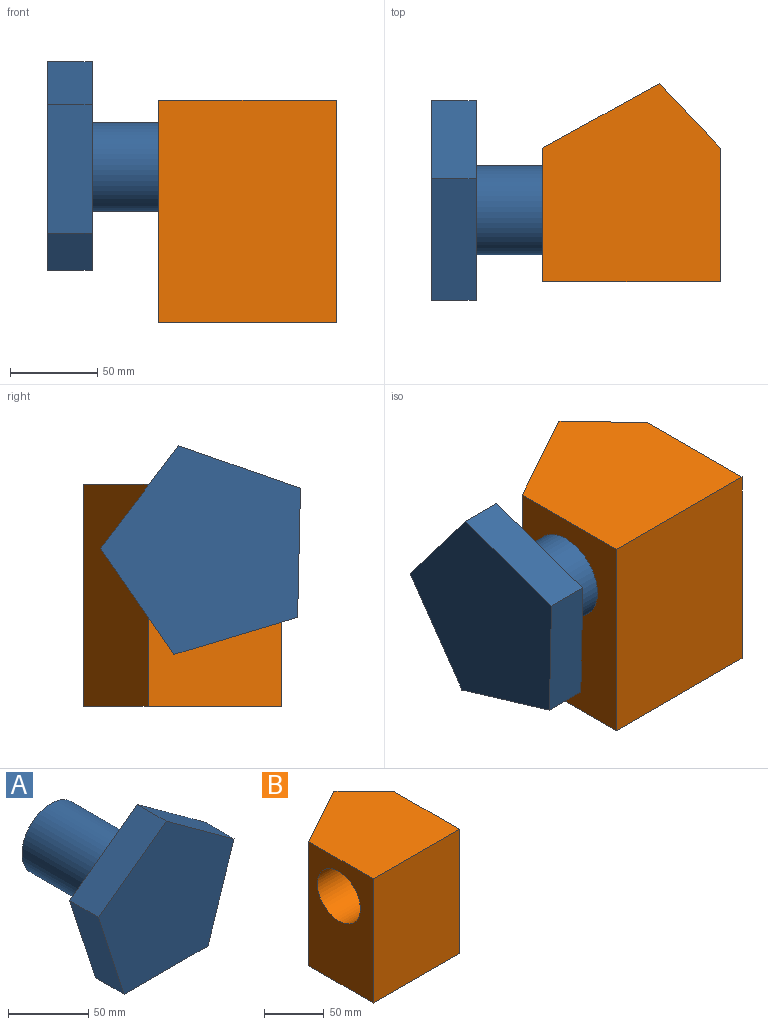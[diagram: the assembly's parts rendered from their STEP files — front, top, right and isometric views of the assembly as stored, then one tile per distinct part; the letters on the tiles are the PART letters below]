
ASSEMBLY  parts=2 mates=1
PART A: 9 faces, bbox 119.4x101.6x113.6 mm
  f0: cylinder r=25.4mm len=76.2mm, axis (0,1,0), area 12161mm2, adj f1,f8
  f1: plane 50.8x50.8mm, normal (0,1,0), area 2026.8mm2, adj f0
  f2: plane 70.2x25.4mm, normal (0.95,0,-0.31), area 1874.9mm2, adj f3,f6,f7,f8
  f3: plane 59.72x43.39mm, normal (0.59,0,0.81), area 1874.9mm2, adj f2,f4,f7,f8
  f4: plane 59.72x43.39mm, normal (-0.59,0,0.81), area 1874.9mm2, adj f3,f5,f7,f8
  f5: plane 70.2x25.4mm, normal (-0.95,0,-0.31), area 1874.9mm2, adj f4,f6,f7,f8
  f6: plane 73.82x25.4mm, normal (0,0,-1), area 1874.9mm2, adj f2,f5,f7,f8
  f7: plane 119.44x113.59mm, normal (0,-1,0), area 9374.7mm2, adj f2,f3,f4,f5,f6
  f8: plane 119.44x113.59mm, normal (0,1,0), area 7347.9mm2, adj f0,f2,f3,f4,f5,f6
PART B: 9 faces, bbox 101.6x113.1x127 mm
  f0: plane 127x76.2mm, normal (1,0,0), area 9677.4mm2, adj f1,f4,f5,f6
  f1: plane 127x36.89mm, normal (0.73,0.69,0), area 6451.6mm2, adj f0,f2,f5,f6
  f2: plane 127x66.68mm, normal (-0.48,0.88,0), area 9677.4mm2, adj f1,f3,f5,f6
  f3: plane 127x76.2mm, normal (-1,0,0), area 7650.6mm2, adj f2,f4,f5,f6,f7
  f4: plane 127x101.6mm, normal (0,-1,0), area 12903.2mm2, adj f0,f3,f5,f6
  f5: plane 113.09x101.6mm, normal (0,0,1), area 9615.9mm2, adj f0,f1,f2,f3,f4
  f6: plane 113.09x101.6mm, normal (0,0,-1), area 9615.9mm2, adj f0,f1,f2,f3,f4
  f7: cylinder r=25.4mm len=50.8mm, axis (-1,0,0), area 8107.3mm2, adj f3,f8
  f8: plane 50.8x50.8mm, normal (-1,0,0), area 2026.8mm2, adj f7
PLACE A rot(axis=(0.42,0.42,-0.8),102.4deg) t=(1.15,33.13,86.95)mm
PLACE B t=(-36.95,-7.51,-1.95)mm fixed
MATE revolute B.f7 <-> A.f0  axis (-1,0,0) through (-36.95,33.13,86.95)mm
